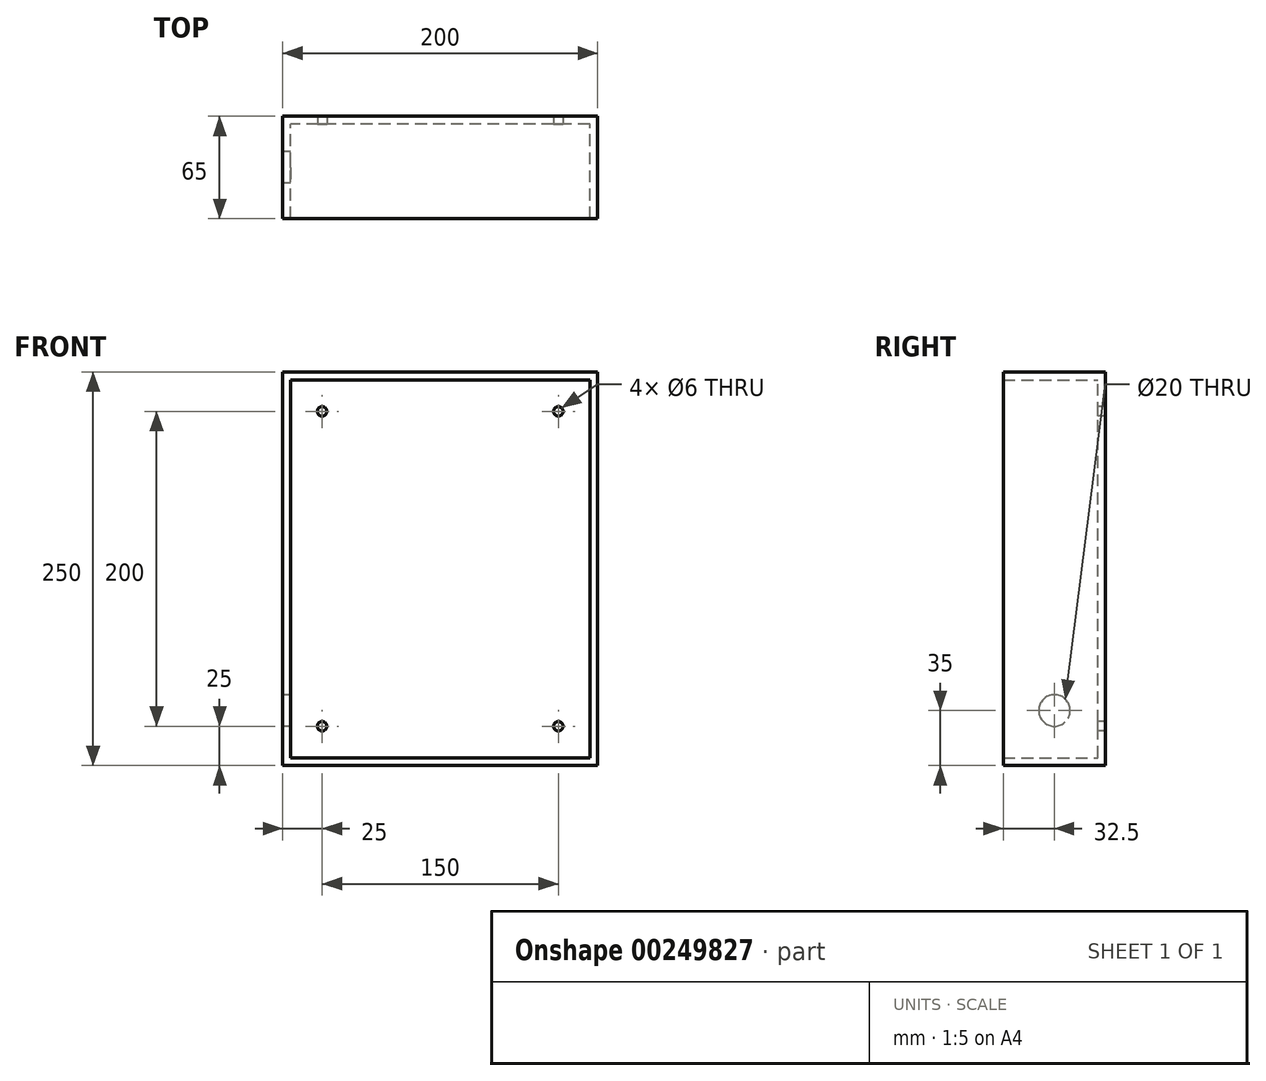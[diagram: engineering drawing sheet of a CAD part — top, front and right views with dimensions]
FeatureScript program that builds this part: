
annotation { "Feature Type Name" : "Feature", "Feature Type Description" : "" }
export const myFeature = defineFeature(function(context is Context, id is Id, definition is map)
    precondition{}
    {
        {
            var Q0;
            Q0=qCreatedBy(makeId("Front.planeOp"),FACE);
            var sketch = newSketch(context, id + "F0", { "sketchPlane" : qUnion([Q0])});
            skLineSegment(sketch, "E0.bottom", {"start": v(100, 125) * mm, "end": v(-100, 125) * mm});
            skLineSegment(sketch, "E0.top", {"start": v(100, -125) * mm, "end": v(-100, -125) * mm});
            skLineSegment(sketch, "E0.left", {"start": v(100, 125) * mm, "end": v(100, -125) * mm});
            skLineSegment(sketch, "E0.right", {"start": v(-100, 125) * mm, "end": v(-100, -125) * mm});
            skPoint(sketch, "E0.middle", {"position": v(0, 0) * mm});
            skSolve(sketch);
        }
        {
            var Q0;
            Q0=makeQuery(id+"F0.imprint","IMPRINT",FACE,{"disambiguationData":[TD([[makeQuery(id+"F0.imprint","IMPRINT",EDGE,{"derivedFrom":sQuery(id+"F0.wireOp",EDGE,"E0.bottom")}),1.0]])]});
            extrude(context, id + "F1", {"entities" : qUnion([Q0]), "depth" : 5 * mm});
        }
        {
            var Q0;
            Q0=makeQuery(id+"F1.opExtrude","CAP_FACE",FACE,{"disambiguationData":[OSD([sQuery(id+"F0.wireOp",EDGE,"E0.bottom"),sQuery(id+"F0.wireOp",EDGE,"E0.top"),sQuery(id+"F0.wireOp",EDGE,"E0.left"),sQuery(id+"F0.wireOp",EDGE,"E0.right")])],"isStart":false});
            var sketch = newSketch(context, id + "F2", { "sketchPlane" : qUnion([Q0])});
            skLineSegment(sketch, "E1.0.0", {"start": v(-100, -125) * mm, "end": v(100, -125) * mm});
            skLineSegment(sketch, "E1.0.1", {"start": v(100, -125) * mm, "end": v(100, 125) * mm});
            skLineSegment(sketch, "E1.0.2", {"start": v(100, 125) * mm, "end": v(-100, 125) * mm});
            skLineSegment(sketch, "E1.0.3", {"start": v(-100, 125) * mm, "end": v(-100, -125) * mm});
            skLineSegment(sketch, "E2.0", {"start": v(95, 120) * mm, "end": v(-95, 120) * mm});
            skLineSegment(sketch, "E2.1", {"start": v(95, -120) * mm, "end": v(95, 120) * mm});
            skLineSegment(sketch, "E2.2", {"start": v(-95, -120) * mm, "end": v(95, -120) * mm});
            skLineSegment(sketch, "E2.3", {"start": v(-95, 120) * mm, "end": v(-95, -120) * mm});
            skSolve(sketch);
        }
        {
            var Q0;
            Q0=makeQuery(id+"F2.imprint","IMPRINT",FACE,{"disambiguationData":[TD([[makeQuery(id+"F2.imprint","IMPRINT",EDGE,{"derivedFrom":sQuery(id+"F2.wireOp",EDGE,"E1.0.0")}),-1.0]])]});
            extrude(context, id + "F3", {"entities" : qUnion([Q0]), "operationType" : NewBodyOperationType.ADD, "depth" : 60 * mm});
        }
        {
            var Q0;
            Q0=makeQuery(id+"F1.opExtrude","CAP_FACE",FACE,{"disambiguationData":[OSD([sQuery(id+"F0.wireOp",EDGE,"E0.bottom"),sQuery(id+"F0.wireOp",EDGE,"E0.top"),sQuery(id+"F0.wireOp",EDGE,"E0.left"),sQuery(id+"F0.wireOp",EDGE,"E0.right")])],"isStart":false});
            var sketch = newSketch(context, id + "F4", { "sketchPlane" : qUnion([Q0])});
            skLineSegment(sketch, "E3.bottom", {"start": v(75, 100) * mm, "end": v(-75, 100) * mm});
            skLineSegment(sketch, "E3.top", {"start": v(75, -100) * mm, "end": v(-75, -100) * mm});
            skLineSegment(sketch, "E3.left", {"start": v(75, 100) * mm, "end": v(75, -100) * mm});
            skLineSegment(sketch, "E3.right", {"start": v(-75, 100) * mm, "end": v(-75, -100) * mm});
            skPoint(sketch, "E3.middle", {"position": v(0, 0) * mm});
            skCircle(sketch, "E4", {"center": v(-75, 100) * mm, "radius": 3 * mm});
            skCircle(sketch, "E5", {"center": v(75, 100) * mm, "radius": 3 * mm});
            skCircle(sketch, "E6", {"center": v(75, -100) * mm, "radius": 3 * mm});
            skCircle(sketch, "E7", {"center": v(-75, -100) * mm, "radius": 3 * mm});
            skSolve(sketch);
        }
        {
            var Q0;
            {var subQ0=sQuery(id+"F4.wireOp",EDGE,"E3.right");var subQ1=sQuery(id+"F4.wireOp",EDGE,"E3.bottom");var subQ2=makeQuery(id+"F4.imprint","INTERSECT",VERTEX,{"derivedFrom":[subQ1,subQ0]});Q0=makeQuery(id+"F4.imprint","IMPRINT",FACE,{"disambiguationData":[TD([[makeQuery(id+"F4.imprint","IMPRINT",EDGE,{"disambiguationData":[TD([[subQ2,1.0]])],"derivedFrom":subQ1}),1.0]])]});}
            var Q1;
            {var subQ0=sQuery(id+"F4.wireOp",EDGE,"E3.right");var subQ1=sQuery(id+"F4.wireOp",EDGE,"E3.bottom");var subQ2=makeQuery(id+"F4.imprint","INTERSECT",VERTEX,{"derivedFrom":[subQ1,subQ0]});Q1=makeQuery(id+"F4.imprint","IMPRINT",FACE,{"disambiguationData":[TD([[makeQuery(id+"F4.imprint","IMPRINT",EDGE,{"disambiguationData":[TD([[subQ2,1.0]])],"derivedFrom":subQ1}),-1.0]])]});}
            var Q2;
            {var subQ0=sQuery(id+"F4.wireOp",EDGE,"E3.left");var subQ1=sQuery(id+"F4.wireOp",EDGE,"E3.bottom");var subQ2=makeQuery(id+"F4.imprint","INTERSECT",VERTEX,{"derivedFrom":[subQ1,subQ0]});Q2=makeQuery(id+"F4.imprint","IMPRINT",FACE,{"disambiguationData":[TD([[makeQuery(id+"F4.imprint","IMPRINT",EDGE,{"disambiguationData":[TD([[subQ2,-1.0]])],"derivedFrom":subQ1}),-1.0]])]});}
            var Q3;
            {var subQ0=sQuery(id+"F4.wireOp",EDGE,"E3.left");var subQ1=sQuery(id+"F4.wireOp",EDGE,"E3.bottom");var subQ2=makeQuery(id+"F4.imprint","INTERSECT",VERTEX,{"derivedFrom":[subQ1,subQ0]});Q3=makeQuery(id+"F4.imprint","IMPRINT",FACE,{"disambiguationData":[TD([[makeQuery(id+"F4.imprint","IMPRINT",EDGE,{"disambiguationData":[TD([[subQ2,-1.0]])],"derivedFrom":subQ1}),1.0]])]});}
            var Q4;
            {var subQ0=sQuery(id+"F4.wireOp",EDGE,"E3.left");var subQ1=sQuery(id+"F4.wireOp",EDGE,"E3.top");var subQ2=makeQuery(id+"F4.imprint","INTERSECT",VERTEX,{"derivedFrom":[subQ1,subQ0]});Q4=makeQuery(id+"F4.imprint","IMPRINT",FACE,{"disambiguationData":[TD([[makeQuery(id+"F4.imprint","IMPRINT",EDGE,{"disambiguationData":[TD([[subQ2,-1.0]])],"derivedFrom":subQ1}),1.0]])]});}
            var Q5;
            {var subQ0=sQuery(id+"F4.wireOp",EDGE,"E3.left");var subQ1=sQuery(id+"F4.wireOp",EDGE,"E3.top");var subQ2=makeQuery(id+"F4.imprint","INTERSECT",VERTEX,{"derivedFrom":[subQ1,subQ0]});Q5=makeQuery(id+"F4.imprint","IMPRINT",FACE,{"disambiguationData":[TD([[makeQuery(id+"F4.imprint","IMPRINT",EDGE,{"disambiguationData":[TD([[subQ2,-1.0]])],"derivedFrom":subQ1}),-1.0]])]});}
            var Q6;
            {var subQ0=sQuery(id+"F4.wireOp",EDGE,"E3.right");var subQ1=sQuery(id+"F4.wireOp",EDGE,"E3.top");var subQ2=makeQuery(id+"F4.imprint","INTERSECT",VERTEX,{"derivedFrom":[subQ1,subQ0]});Q6=makeQuery(id+"F4.imprint","IMPRINT",FACE,{"disambiguationData":[TD([[makeQuery(id+"F4.imprint","IMPRINT",EDGE,{"disambiguationData":[TD([[subQ2,1.0]])],"derivedFrom":subQ1}),1.0]])]});}
            var Q7;
            {var subQ0=sQuery(id+"F4.wireOp",EDGE,"E3.right");var subQ1=sQuery(id+"F4.wireOp",EDGE,"E3.top");var subQ2=makeQuery(id+"F4.imprint","INTERSECT",VERTEX,{"derivedFrom":[subQ1,subQ0]});Q7=makeQuery(id+"F4.imprint","IMPRINT",FACE,{"disambiguationData":[TD([[makeQuery(id+"F4.imprint","IMPRINT",EDGE,{"disambiguationData":[TD([[subQ2,1.0]])],"derivedFrom":subQ1}),-1.0]])]});}
            extrude(context, id + "F5", {"entities" : qUnion([Q0, Q1, Q2, Q3, Q4, Q5, Q6, Q7]), "operationType" : NewBodyOperationType.REMOVE, "endBound" : BoundingType.THROUGH_ALL, "oppositeDirection" : true, "depth" : 25 * mm});
        }
        {
            var Q0;
            Q0=makeQuery(id+"F3.boolean.opBoolean","MERGE",FACE,{"derivedFrom":[makeQuery(id+"F1.opExtrude","SWEPT_FACE",FACE,{"disambiguationData":[OSD([sQuery(id+"F0.wireOp",EDGE,"E0.right")])]}),makeQuery(id+"F3.opExtrude","SWEPT_FACE",FACE,{"disambiguationData":[OSD([sQuery(id+"F2.wireOp",EDGE,"E1.0.3")])]})]});
            var sketch = newSketch(context, id + "F6", { "sketchPlane" : qUnion([Q0])});
            skCircle(sketch, "E8", {"center": v(32.5, -90) * mm, "radius": 10 * mm});
            skPoint(sketch, "E8.centerSnap0", {"position": v(32.5, -125) * mm});
            skSolve(sketch);
        }
        {
            var Q0;
            Q0=makeQuery(id+"F6.imprint","IMPRINT",FACE,{"disambiguationData":[TD([[makeQuery(id+"F6.imprint","IMPRINT",EDGE,{"derivedFrom":sQuery(id+"F6.wireOp",EDGE,"E8")}),1.0]])]});
            extrude(context, id + "F7", {"entities" : qUnion([Q0]), "operationType" : NewBodyOperationType.REMOVE, "oppositeDirection" : true, "depth" : 25 * mm});
        }
    });
